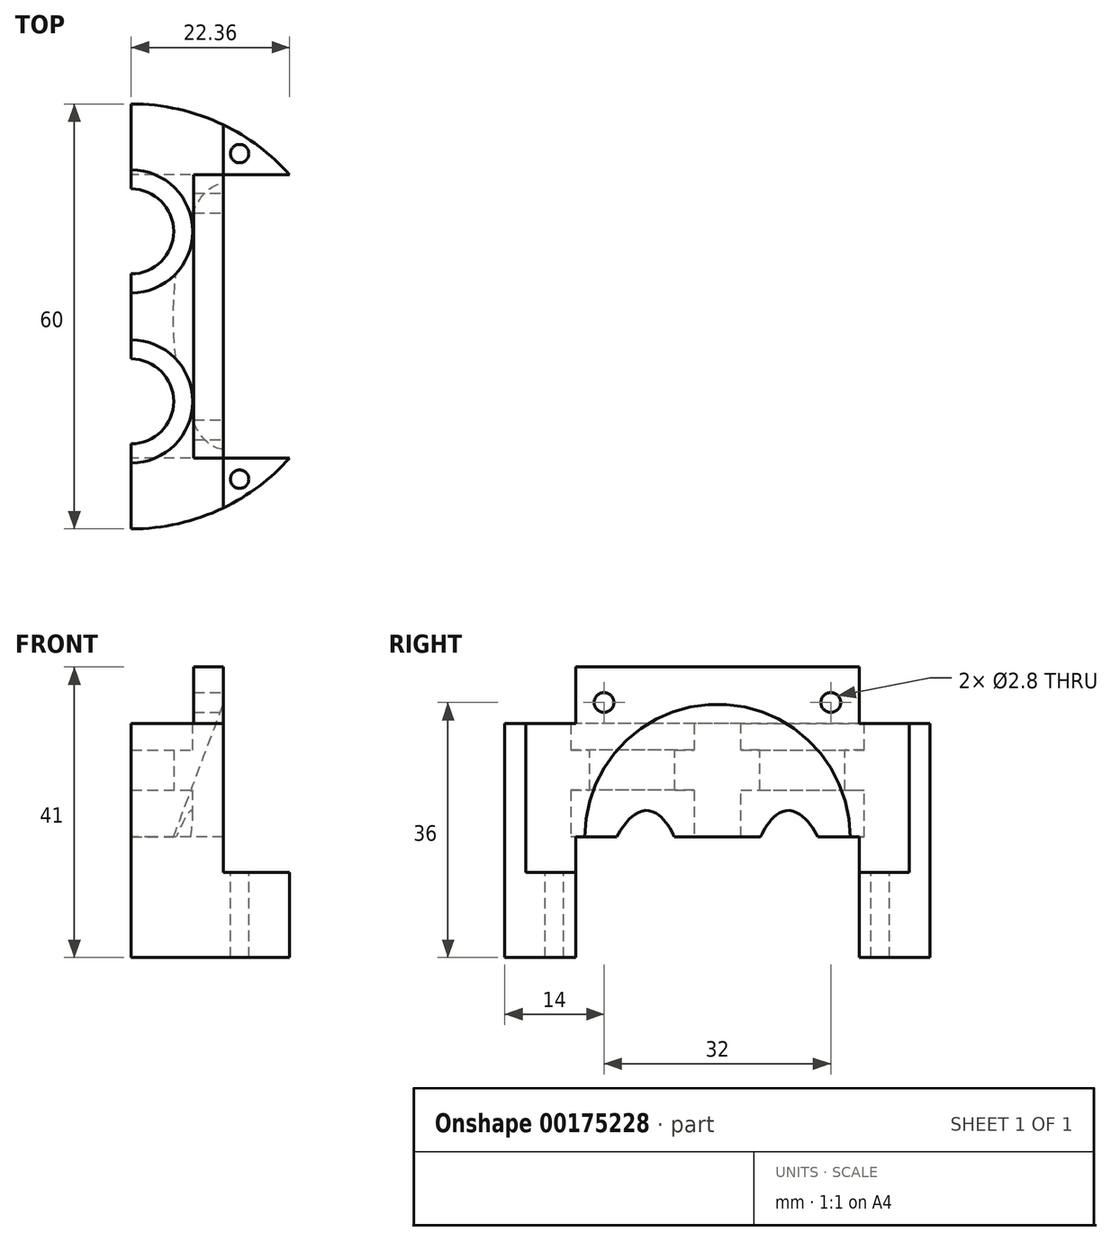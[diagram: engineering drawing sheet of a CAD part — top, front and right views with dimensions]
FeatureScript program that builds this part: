
annotation { "Feature Type Name" : "Feature", "Feature Type Description" : "" }
export const myFeature = defineFeature(function(context is Context, id is Id, definition is map)
    precondition{}
    {
        {
            var Q0;
            Q0=qCreatedBy(makeId("Top.planeOp"),FACE);
            var sketch = newSketch(context, id + "F0", { "sketchPlane" : qUnion([Q0])});
            skLineSegment(sketch, "E0.bottom", {"start": v(-13, -12) * mm, "end": v(13, -12) * mm});
            skLineSegment(sketch, "E0.top", {"start": v(-13, 12) * mm, "end": v(13, 12) * mm});
            skLineSegment(sketch, "E0.left", {"start": v(-13, -12) * mm, "end": v(-13, 12) * mm});
            skLineSegment(sketch, "E0.right", {"start": v(13, -12) * mm, "end": v(13, 12) * mm});
            skPoint(sketch, "E0.middle", {"position": v(0, 0) * mm});
            skCircle(sketch, "E1", {"center": v(0, 0) * mm, "radius": 20 * mm, "construction": true});
            skLineSegment(sketch, "E2", {"start": v(-31.1, 0) * mm, "end": v(39.02, 0) * mm, "construction": true});
            skCircle(sketch, "E3", {"center": v(0, 0) * mm, "radius": 30 * mm});
            skCircle(sketch, "E4", {"center": v(0, 12) * mm, "radius": 6 * mm});
            skCircle(sketch, "E5", {"center": v(0, -12) * mm, "radius": 6 * mm});
            skLineSegment(sketch, "E6.bottom", {"start": v(-13, 27.04) * mm, "end": v(13, 27.04) * mm});
            skLineSegment(sketch, "E6.top", {"start": v(-13, -27.04) * mm, "end": v(13, -27.04) * mm});
            skLineSegment(sketch, "E6.left", {"start": v(-13, 27.04) * mm, "end": v(-13, -27.04) * mm});
            skLineSegment(sketch, "E6.right", {"start": v(13, 27.04) * mm, "end": v(13, -27.04) * mm});
            skSolve(sketch);
        }
        {
            var Q0;
            {var subQ0=sQuery(id+"F0.wireOp",EDGE,"E6.bottom");Q0=makeQuery(id+"F0.imprint","IMPRINT",FACE,{"disambiguationData":[TD([[makeQuery(id+"F0.imprint","IMPRINT",EDGE,{"derivedFrom":subQ0}),1.0]])]});}
            var Q1;
            {var subQ0=sQuery(id+"F0.wireOp",EDGE,"E6.top");Q1=makeQuery(id+"F0.imprint","IMPRINT",FACE,{"disambiguationData":[TD([[makeQuery(id+"F0.imprint","IMPRINT",EDGE,{"derivedFrom":subQ0}),-1.0]])]});}
            var Q2;
            {var subQ0=sQuery(id+"F0.wireOp",EDGE,"E6.top");Q2=makeQuery(id+"F0.imprint","IMPRINT",FACE,{"disambiguationData":[TD([[makeQuery(id+"F0.imprint","IMPRINT",EDGE,{"derivedFrom":subQ0}),1.0]])]});}
            var Q3;
            {var subQ6=sQuery(id+"F0.wireOp",EDGE,"E0.bottom");var subQ9=sQuery(id+"F0.wireOp",EDGE,"E6.left");var subQ13=makeQuery(id+"F0.imprint","INTERSECT",VERTEX,{"derivedFrom":[subQ6,subQ9]});Q3=makeQuery(id+"F0.imprint","IMPRINT",FACE,{"disambiguationData":[TD([[makeQuery(id+"F0.imprint","IMPRINT",EDGE,{"disambiguationData":[TD([[subQ13,-1.0]])],"derivedFrom":subQ6}),1.0]])]});}
            var Q4;
            {var subQ0=sQuery(id+"F0.wireOp",EDGE,"E6.bottom");Q4=makeQuery(id+"F0.imprint","IMPRINT",FACE,{"disambiguationData":[TD([[makeQuery(id+"F0.imprint","IMPRINT",EDGE,{"derivedFrom":subQ0}),-1.0]])]});}
            extrude(context, id + "F1", {"entities" : qUnion([Q0, Q1, Q2, Q3, Q4]), "depth" : 33 * mm});
        }
        {
            var Q0;
            Q0=qCreatedBy(makeId("Top.planeOp"),FACE);
            var sketch = newSketch(context, id + "F2", { "sketchPlane" : qUnion([Q0])});
            skCircle(sketch, "E7", {"center": v(0, 0) * mm, "radius": 30 * mm});
            skCircle(sketch, "E8", {"center": v(-26.68, -13.72) * mm, "radius": 7.63 * mm});
            skLineSegment(sketch, "E9", {"start": v(-22.36, -20) * mm, "end": v(-12.88, -20) * mm});
            skLineSegment(sketch, "E10", {"start": v(-12.88, -20) * mm, "end": v(22.36, -20) * mm});
            skLineSegment(sketch, "E11", {"start": v(22.36, -20) * mm, "end": v(-53.5, 0) * mm, "construction": true});
            skLineSegment(sketch, "E12", {"start": v(-53.5, 0) * mm, "end": v(57.64, 0) * mm, "construction": true});
            skLineSegment(sketch, "E13.MirrorCS", {"start": v(-12.88, 20) * mm, "end": v(22.36, 20) * mm});
            skLineSegment(sketch, "E14.MirrorCS", {"start": v(-22.36, 20) * mm, "end": v(-12.88, 20) * mm});
            skSolve(sketch);
        }
        {
            var Q0;
            {var subQ0=sQuery(id+"F2.wireOp",EDGE,"E13.MirrorCS");Q0=makeQuery(id+"F2.imprint","IMPRINT",FACE,{"disambiguationData":[TD([[makeQuery(id+"F2.imprint","IMPRINT",EDGE,{"derivedFrom":subQ0}),1.0]])]});}
            var Q1;
            {var subQ0=sQuery(id+"F2.wireOp",EDGE,"E9");Q1=makeQuery(id+"F2.imprint","IMPRINT",FACE,{"disambiguationData":[TD([[makeQuery(id+"F2.imprint","IMPRINT",EDGE,{"derivedFrom":subQ0}),-1.0]])]});}
            extrude(context, id + "F3", {"entities" : qUnion([Q0, Q1]), "operationType" : NewBodyOperationType.ADD, "depth" : 12 * mm});
        }
        {
            var Q0;
            Q0=makeQuery(id+"F1.opExtrude","CAP_FACE",FACE,{"disambiguationData":[OSD([sQuery(id+"F0.wireOp",EDGE,"E3"),sQuery(id+"F0.wireOp",EDGE,"E4"),sQuery(id+"F0.wireOp",EDGE,"E5"),sQuery(id+"F0.wireOp",EDGE,"E6.left"),sQuery(id+"F0.wireOp",EDGE,"E6.right")])],"isStart":false});
            var sketch = newSketch(context, id + "F4", { "sketchPlane" : qUnion([Q0])});
            skLineSegment(sketch, "E15", {"start": v(0, 35.89) * mm, "end": v(0, -37.95) * mm});
            skPoint(sketch, "E15.endSnap0", {"position": v(0, 30) * mm});
            skLineSegment(sketch, "E16", {"start": v(0, -37.95) * mm, "end": v(28.6, -37.95) * mm});
            skLineSegment(sketch, "E17", {"start": v(28.6, -37.95) * mm, "end": v(28.6, 36.6) * mm});
            skLineSegment(sketch, "E18", {"start": v(28.6, 36.6) * mm, "end": v(0, 36.6) * mm});
            skLineSegment(sketch, "E19", {"start": v(0, 36.6) * mm, "end": v(0, 33.04) * mm});
            skSolve(sketch);
        }
        {
            var Q0;
            Q0=makeQuery(id+"F1.opExtrude","SWEPT_FACE",FACE,{"disambiguationData":[OSD([sQuery(id+"F0.wireOp",EDGE,"E6.left")])]});
            var sketch = newSketch(context, id + "F5", { "sketchPlane" : qUnion([Q0])});
            skLineSegment(sketch, "E20.bottom", {"start": v(-20, 0) * mm, "end": v(20, 0) * mm});
            skLineSegment(sketch, "E20.top", {"start": v(-20, 17) * mm, "end": v(20, 17) * mm});
            skLineSegment(sketch, "E20.left", {"start": v(-20, 0) * mm, "end": v(-20, 17) * mm});
            skLineSegment(sketch, "E20.right", {"start": v(20, 0) * mm, "end": v(20, 17) * mm});
            skSolve(sketch);
        }
        {
            var Q0;
            {var subQ5=sQuery(id+"F5.wireOp",EDGE,"E20.bottom");Q0=makeQuery(id+"F5.imprint","IMPRINT",FACE,{"disambiguationData":[TD([[makeQuery(id+"F5.imprint","IMPRINT",EDGE,{"derivedFrom":subQ5}),1.0]])]});}
            extrude(context, id + "F6", {"entities" : qUnion([Q0]), "operationType" : NewBodyOperationType.REMOVE, "endBound" : BoundingType.THROUGH_ALL, "oppositeDirection" : true, "depth" : 25 * mm});
        }
        {
            var Q0;
            Q0=makeQuery(id+"F6.boolean.opBoolean","COPY",FACE,{"derivedFrom":makeQuery(id+"F6.opExtrude","SWEPT_FACE",FACE,{"disambiguationData":[OSD([sQuery(id+"F5.wireOp",EDGE,"E20.top")])]})});
            var sketch = newSketch(context, id + "F7", { "sketchPlane" : qUnion([Q0])});
            skCircle(sketch, "E21", {"center": v(0, 12) * mm, "radius": 11.29 * mm, "construction": true});
            skCircle(sketch, "E22", {"center": v(0, -12) * mm, "radius": 11.29 * mm, "construction": true});
            skCircle(sketch, "E23", {"center": v(0, 12) * mm, "radius": 11.29 * mm});
            skCircle(sketch, "E24", {"center": v(0, -12) * mm, "radius": 11.29 * mm});
            skSolve(sketch);
        }
        {
            var Q0;
            Q0=makeQuery(id+"F7.imprint","IMPRINT",FACE,{"disambiguationData":[TD([[makeQuery(id+"F7.imprint","IMPRINT",EDGE,{"derivedFrom":makeQuery(id+"F6.boolean.opBoolean","INTERSECT",EDGE,{"derivedFrom":[makeQuery(id+"F1.opExtrude","SWEPT_FACE",FACE,{"disambiguationData":[OSD([sQuery(id+"F0.wireOp",EDGE,"E4")])]}),makeQuery(id+"F6.opExtrude","SWEPT_FACE",FACE,{"disambiguationData":[OSD([sQuery(id+"F5.wireOp",EDGE,"E20.top")])]})]})}),1.0]])]});
            var Q1;
            Q1=makeQuery(id+"F7.imprint","IMPRINT",FACE,{"disambiguationData":[TD([[makeQuery(id+"F7.imprint","IMPRINT",EDGE,{"derivedFrom":makeQuery(id+"F6.boolean.opBoolean","INTERSECT",EDGE,{"derivedFrom":[makeQuery(id+"F1.opExtrude","SWEPT_FACE",FACE,{"disambiguationData":[OSD([sQuery(id+"F0.wireOp",EDGE,"E5")])]}),makeQuery(id+"F6.opExtrude","SWEPT_FACE",FACE,{"disambiguationData":[OSD([sQuery(id+"F5.wireOp",EDGE,"E20.top")])]})]})}),1.0]])]});
            var Q2;
            {var subQ0=sQuery(id+"F7.wireOp",EDGE,"E23");var subQ1=makeQuery(id+"F6.boolean.opBoolean","COPY",EDGE,{"derivedFrom":makeQuery(id+"F6.opExtrude","SWEPT_EDGE",EDGE,{"disambiguationData":[OSD([sQuery(id+"F5.wireOp",EDGE,"E20.top"),sQuery(id+"F5.wireOp",EDGE,"E20.right")])]})});var subQ2=makeQuery(id+"F7.imprint","INTERSECT",VERTEX,{"disambiguationData":[OD(0.0)],"derivedFrom":[subQ1,subQ0]});Q2=makeQuery(id+"F7.imprint","IMPRINT",FACE,{"disambiguationData":[TD([[makeQuery(id+"F7.imprint","IMPRINT",EDGE,{"disambiguationData":[TD([[subQ2,1.0]])],"derivedFrom":subQ0}),1.0]])]});}
            var Q3;
            {var subQ0=sQuery(id+"F7.wireOp",EDGE,"E24");var subQ1=makeQuery(id+"F6.boolean.opBoolean","COPY",EDGE,{"derivedFrom":makeQuery(id+"F6.opExtrude","SWEPT_EDGE",EDGE,{"disambiguationData":[OSD([sQuery(id+"F5.wireOp",EDGE,"E20.top"),sQuery(id+"F5.wireOp",EDGE,"E20.left")])]})});var subQ2=makeQuery(id+"F7.imprint","INTERSECT",VERTEX,{"disambiguationData":[OD(0.0)],"derivedFrom":[subQ1,subQ0]});Q3=makeQuery(id+"F7.imprint","IMPRINT",FACE,{"disambiguationData":[TD([[makeQuery(id+"F7.imprint","IMPRINT",EDGE,{"disambiguationData":[TD([[subQ2,-1.0]])],"derivedFrom":subQ0}),1.0]])]});}
            var Q4;
            {var subQ1=sQuery(id+"F5.wireOp",EDGE,"E20.top");Q4=makeQuery(id+"F7.imprint","IMPRINT",FACE,{"disambiguationData":[TD([[makeQuery(id+"F7.imprint","IMPRINT",EDGE,{"derivedFrom":makeQuery(id+"F6.boolean.opBoolean","INTERSECT",EDGE,{"derivedFrom":[makeQuery(id+"F1.opExtrude","SWEPT_FACE",FACE,{"disambiguationData":[OSD([sQuery(id+"F0.wireOp",EDGE,"E5")])]}),makeQuery(id+"F6.opExtrude","SWEPT_FACE",FACE,{"disambiguationData":[OSD([subQ1])]})]})}),-1.0]])]});}
            extrude(context, id + "F8", {"entities" : qUnion([Q0, Q1, Q2, Q3, Q4]), "operationType" : NewBodyOperationType.REMOVE, "endBound" : BoundingType.THROUGH_ALL, "depth" : 25 * mm});
        }
        {
            var Q0;
            {var subQ0=sQuery(id+"F0.wireOp",EDGE,"E6.right");var subQ1=makeQuery(id+"F1.opExtrude","CAP_EDGE",EDGE,{"disambiguationData":[OSD([subQ0])],"isStart":false});Q0=makeQuery(id+"F4.imprint","IMPRINT",FACE,{"disambiguationData":[TD([[makeQuery(id+"F4.imprint","IMPRINT",EDGE,{"derivedFrom":subQ1}),-1.0]])]});}
            var sketch = newSketch(context, id + "F9", { "sketchPlane" : qUnion([Q0])});
            skLineSegment(sketch, "E25.bottom", {"start": v(13, 20) * mm, "end": v(-13, 20) * mm});
            skLineSegment(sketch, "E25.top", {"start": v(13, -20) * mm, "end": v(-13, -20) * mm});
            skLineSegment(sketch, "E25.left", {"start": v(13, 20) * mm, "end": v(13, -20) * mm});
            skLineSegment(sketch, "E25.right", {"start": v(-13, 20) * mm, "end": v(-13, -20) * mm});
            skPoint(sketch, "E25.middle", {"position": v(0, 0) * mm});
            skLineSegment(sketch, "E26.bottom", {"start": v(8.83, 20) * mm, "end": v(17.17, 20) * mm});
            skLineSegment(sketch, "E26.top", {"start": v(8.83, -20) * mm, "end": v(17.17, -20) * mm});
            skLineSegment(sketch, "E26.left", {"start": v(8.83, 20) * mm, "end": v(8.83, -20) * mm});
            skLineSegment(sketch, "E26.right", {"start": v(17.17, 20) * mm, "end": v(17.17, -20) * mm});
            skPoint(sketch, "E26.middle", {"position": v(13, 0) * mm});
            skSolve(sketch);
        }
        {
            var Q0;
            {var subQ0=sQuery(id+"F9.wireOp",EDGE,"E26.left");Q0=makeQuery(id+"F9.imprint","IMPRINT",FACE,{"disambiguationData":[TD([[makeQuery(id+"F9.imprint","IMPRINT",EDGE,{"derivedFrom":subQ0}),1.0]])]});}
            extrude(context, id + "F10", {"entities" : qUnion([Q0]), "operationType" : NewBodyOperationType.ADD, "depth" : 8 * mm});
        }
        {
            var Q0;
            {var subQ0=sQuery(id+"F0.wireOp",EDGE,"E6.right");Q0=makeQuery(id+"F10.boolean.opBoolean","MERGE",FACE,{"derivedFrom":[makeQuery(id+"F1.opExtrude","SWEPT_FACE",FACE,{"disambiguationData":[OSD([subQ0])]}),makeQuery(id+"F10.opExtrude","SWEPT_FACE",FACE,{"disambiguationData":[OSD([subQ0])]})]});}
            var sketch = newSketch(context, id + "F11", { "sketchPlane" : qUnion([Q0])});
            skLineSegment(sketch, "E27.bottom", {"start": v(-20, 41) * mm, "end": v(20, 41) * mm});
            skLineSegment(sketch, "E27.top", {"start": v(-20, 0) * mm, "end": v(20, 0) * mm});
            skLineSegment(sketch, "E27.left", {"start": v(-20, 41) * mm, "end": v(-20, 0) * mm});
            skLineSegment(sketch, "E27.right", {"start": v(20, 41) * mm, "end": v(20, 0) * mm});
            skLineSegment(sketch, "E28", {"start": v(-20, 36) * mm, "end": v(20, 36) * mm, "construction": true});
            skCircle(sketch, "E29", {"center": v(-16, 36) * mm, "radius": 1.4 * mm});
            skCircle(sketch, "E30", {"center": v(16, 36) * mm, "radius": 1.4 * mm});
            skSolve(sketch);
        }
        {
            var Q0;
            Q0=makeQuery(id+"F11.imprint","IMPRINT",FACE,{"disambiguationData":[TD([[makeQuery(id+"F11.imprint","IMPRINT",EDGE,{"derivedFrom":sQuery(id+"F11.wireOp",EDGE,"E29")}),1.0]])]});
            var Q1;
            Q1=makeQuery(id+"F11.imprint","IMPRINT",FACE,{"disambiguationData":[TD([[makeQuery(id+"F11.imprint","IMPRINT",EDGE,{"derivedFrom":sQuery(id+"F11.wireOp",EDGE,"E30")}),1.0]])]});
            extrude(context, id + "F12", {"entities" : qUnion([Q0, Q1]), "operationType" : NewBodyOperationType.REMOVE, "endBound" : BoundingType.THROUGH_ALL, "oppositeDirection" : true, "depth" : 25 * mm});
        }
        {
            var Q0;
            {var subQ0=sQuery(id+"F0.wireOp",EDGE,"E6.left");var subQ1=makeQuery(id+"F1.opExtrude","CAP_EDGE",EDGE,{"disambiguationData":[OSD([subQ0])],"isStart":false});Q0=makeQuery(id+"F4.imprint","IMPRINT",FACE,{"disambiguationData":[TD([[makeQuery(id+"F4.imprint","IMPRINT",EDGE,{"derivedFrom":subQ1}),1.0]])]});}
            var sketch = newSketch(context, id + "F13", { "sketchPlane" : qUnion([Q0])});
            skLineSegment(sketch, "E31", {"start": v(0, 33.3) * mm, "end": v(0, -31.46) * mm});
            skLineSegment(sketch, "E32", {"start": v(0, -31.46) * mm, "end": v(26.28, -31.46) * mm});
            skLineSegment(sketch, "E33", {"start": v(26.28, -31.46) * mm, "end": v(26.28, 32.75) * mm});
            skLineSegment(sketch, "E34", {"start": v(26.28, 32.75) * mm, "end": v(0, 32.75) * mm});
            skLineSegment(sketch, "E35.MirrorCS", {"start": v(-26.28, -31.46) * mm, "end": v(-26.28, 32.75) * mm});
            skLineSegment(sketch, "E36.MirrorCS", {"start": v(-26.28, 32.75) * mm, "end": v(0, 32.75) * mm});
            skLineSegment(sketch, "E37.MirrorCS", {"start": v(0, -31.46) * mm, "end": v(-26.28, -31.46) * mm});
            skSolve(sketch);
        }
        {
            var Q0;
            Q0=makeQuery(id+"F13.imprint","IMPRINT",FACE,{"disambiguationData":[TD([[makeQuery(id+"F13.imprint","IMPRINT",EDGE,{"derivedFrom":sQuery(id+"F13.wireOp",EDGE,"E35.MirrorCS")}),-1.0]])]});
            var Q1;
            {var subQ0=sQuery(id+"F0.wireOp",EDGE,"E6.left");var subQ1=makeQuery(id+"F1.opExtrude","CAP_EDGE",EDGE,{"disambiguationData":[OSD([subQ0])],"isStart":false});Q1=makeQuery(id+"F4.imprint","IMPRINT",FACE,{"disambiguationData":[TD([[makeQuery(id+"F4.imprint","IMPRINT",EDGE,{"derivedFrom":subQ1}),1.0]])]});}
            extrude(context, id + "F14", {"entities" : qUnion([Q0, Q1]), "operationType" : NewBodyOperationType.REMOVE, "endBound" : BoundingType.THROUGH_ALL, "oppositeDirection" : true, "depth" : 25 * mm});
        }
        {
            var Q0;
            {var subQ0=sQuery(id+"F4.wireOp",EDGE,"E15");Q0=makeQuery(id+"F14.boolean.opBoolean","COPY",FACE,{"derivedFrom":makeQuery(id+"F14.opExtrude","SWEPT_FACE",FACE,{"disambiguationData":[OSD([subQ0]),TDD([makeQuery(id+"F4.imprint","IMPRINT",EDGE,{"disambiguationData":[TD([[makeQuery(id+"F4.imprint","INTERSECT",VERTEX,{"disambiguationData":[OD(1.0)],"derivedFrom":[makeQuery(id+"F1.opExtrude","CAP_EDGE",EDGE,{"disambiguationData":[OSD([sQuery(id+"F0.wireOp",EDGE,"E4")])],"isStart":false}),subQ0]}),-1.0]])],"derivedFrom":subQ0})])]})});}
            var sketch = newSketch(context, id + "F15", { "sketchPlane" : qUnion([Q0])});
            skLineSegment(sketch, "E38.bottom", {"start": v(-6, 17) * mm, "end": v(6, 17) * mm});
            skLineSegment(sketch, "E38.top", {"start": v(-6, 49) * mm, "end": v(6, 49) * mm});
            skLineSegment(sketch, "E38.left", {"start": v(-6, 17) * mm, "end": v(-6, 49) * mm});
            skLineSegment(sketch, "E38.right", {"start": v(6, 17) * mm, "end": v(6, 49) * mm});
            skPoint(sketch, "E38.middle", {"position": v(0, 33) * mm});
            skLineSegment(sketch, "E39.bottom", {"start": v(12, 17) * mm, "end": v(-12, 17) * mm});
            skLineSegment(sketch, "E39.top", {"start": v(12, 49) * mm, "end": v(-12, 49) * mm});
            skLineSegment(sketch, "E39.left", {"start": v(12, 17) * mm, "end": v(12, 49) * mm});
            skLineSegment(sketch, "E39.right", {"start": v(-12, 17) * mm, "end": v(-12, 49) * mm});
            skLineSegment(sketch, "E40.bottom", {"start": v(12, 29.31) * mm, "end": v(-12, 29.31) * mm});
            skLineSegment(sketch, "E40.top", {"start": v(12, 36.7) * mm, "end": v(-12, 36.7) * mm});
            skLineSegment(sketch, "E40.left", {"start": v(12, 29.31) * mm, "end": v(12, 36.7) * mm});
            skLineSegment(sketch, "E40.right", {"start": v(-12, 29.31) * mm, "end": v(-12, 36.7) * mm});
            skLineSegment(sketch, "E41.bottom", {"start": v(-12, 33) * mm, "end": v(-3.3, 33) * mm});
            skLineSegment(sketch, "E41.top", {"start": v(-12, 29.31) * mm, "end": v(-3.3, 29.31) * mm});
            skLineSegment(sketch, "E41.left", {"start": v(-12, 33) * mm, "end": v(-12, 29.31) * mm});
            skLineSegment(sketch, "E41.right", {"start": v(-3.3, 33) * mm, "end": v(-3.3, 29.31) * mm});
            skLineSegment(sketch, "E42.bottom", {"start": v(-12, 23.6) * mm, "end": v(-3.31, 23.6) * mm});
            skLineSegment(sketch, "E42.top", {"start": v(-12, 17) * mm, "end": v(-3.3, 17) * mm});
            skLineSegment(sketch, "E42.left", {"start": v(-12, 23.6) * mm, "end": v(-12, 17) * mm});
            skLineSegment(sketch, "E42.right", {"start": v(-3.31, 23.6) * mm, "end": v(-3.31, 17) * mm});
            skLineSegment(sketch, "E43", {"start": v(-3.3, 33) * mm, "end": v(-12, 33) * mm});
            skLineSegment(sketch, "E44", {"start": v(-3.31, 23.6) * mm, "end": v(-12, 23.6) * mm});
            skSolve(sketch);
        }
        {
            var Q0;
            {var subQ5=sQuery(id+"F15.wireOp",EDGE,"E41.right");Q0=makeQuery(id+"F15.imprint","IMPRINT",FACE,{"disambiguationData":[TD([[makeQuery(id+"F15.imprint","IMPRINT",EDGE,{"derivedFrom":subQ5}),-1.0]])]});}
            var Q1;
            {var subQ5=sQuery(id+"F15.wireOp",EDGE,"E42.right");Q1=makeQuery(id+"F15.imprint","IMPRINT",FACE,{"disambiguationData":[TD([[makeQuery(id+"F15.imprint","IMPRINT",EDGE,{"derivedFrom":subQ5}),-1.0]])]});}
            var Q2;
            Q2=sQuery(id+"F15.wireOp",EDGE,"E39.right");
            revolve(context, id + "F16", {"operationType" : NewBodyOperationType.REMOVE, "entities" : qUnion([Q0, Q1]), "axis" : qUnion([Q2]), "revolveType" : RevolveType.FULL, "oppositeDirection" : true});
        }
        {
            var Q0;
            {var subQ0=sQuery(id+"F4.wireOp",EDGE,"E15");Q0=makeQuery(id+"F14.boolean.opBoolean","COPY",FACE,{"derivedFrom":makeQuery(id+"F14.opExtrude","SWEPT_FACE",FACE,{"disambiguationData":[OSD([subQ0]),TDD([makeQuery(id+"F4.imprint","IMPRINT",EDGE,{"disambiguationData":[TD([[makeQuery(id+"F4.imprint","INTERSECT",VERTEX,{"disambiguationData":[OD(1.0)],"derivedFrom":[makeQuery(id+"F1.opExtrude","CAP_EDGE",EDGE,{"disambiguationData":[OSD([sQuery(id+"F0.wireOp",EDGE,"E4")])],"isStart":false}),subQ0]}),-1.0]])],"derivedFrom":subQ0})])]})});}
            var sketch = newSketch(context, id + "F17", { "sketchPlane" : qUnion([Q0])});
            skLineSegment(sketch, "E45.bottom", {"start": v(-6, 29.31) * mm, "end": v(6, 29.31) * mm});
            skLineSegment(sketch, "E45.top", {"start": v(-6, 23.6) * mm, "end": v(6, 23.6) * mm});
            skLineSegment(sketch, "E45.left", {"start": v(-6, 29.31) * mm, "end": v(-6, 23.6) * mm});
            skLineSegment(sketch, "E45.right", {"start": v(6, 29.31) * mm, "end": v(6, 23.6) * mm});
            skLineSegment(sketch, "E46.bottom", {"start": v(0, 23.6) * mm, "end": v(12, 23.6) * mm});
            skLineSegment(sketch, "E46.top", {"start": v(0, 17) * mm, "end": v(12, 17) * mm});
            skLineSegment(sketch, "E46.left", {"start": v(0, 23.6) * mm, "end": v(0, 17) * mm});
            skLineSegment(sketch, "E46.right", {"start": v(12, 23.6) * mm, "end": v(12, 17) * mm});
            skLineSegment(sketch, "E47.bottom", {"start": v(12, 23.6) * mm, "end": v(3.3, 23.6) * mm});
            skLineSegment(sketch, "E47.top", {"start": v(12, 17) * mm, "end": v(3.3, 17) * mm});
            skLineSegment(sketch, "E47.right", {"start": v(3.3, 23.6) * mm, "end": v(3.3, 17) * mm});
            skLineSegment(sketch, "E48.bottom", {"start": v(3.3, 29.31) * mm, "end": v(12, 29.31) * mm});
            skLineSegment(sketch, "E48.top", {"start": v(3.3, 33) * mm, "end": v(12, 33) * mm});
            skLineSegment(sketch, "E48.left", {"start": v(3.3, 29.31) * mm, "end": v(3.3, 33) * mm});
            skLineSegment(sketch, "E48.right", {"start": v(12, 29.31) * mm, "end": v(12, 33) * mm});
            skLineSegment(sketch, "E49", {"start": v(12, 33) * mm, "end": v(12, 15.28) * mm});
            skLineSegment(sketch, "E50", {"start": v(12, 15.28) * mm, "end": v(12, 23.6) * mm});
            skLineSegment(sketch, "E51", {"start": v(12, 17) * mm, "end": v(12, 29.31) * mm});
            skLineSegment(sketch, "E52", {"start": v(12, 33) * mm, "end": v(12, 29.31) * mm});
            skSolve(sketch);
        }
        {
            var Q0;
            {var subQ6=sQuery(id+"F17.wireOp",EDGE,"E48.left");Q0=makeQuery(id+"F17.imprint","IMPRINT",FACE,{"disambiguationData":[TD([[makeQuery(id+"F17.imprint","IMPRINT",EDGE,{"derivedFrom":subQ6}),-1.0]])]});}
            var Q1;
            {var subQ5=sQuery(id+"F17.wireOp",EDGE,"E47.right");Q1=makeQuery(id+"F17.imprint","IMPRINT",FACE,{"disambiguationData":[TD([[makeQuery(id+"F17.imprint","IMPRINT",EDGE,{"derivedFrom":subQ5}),1.0]])]});}
            var Q2;
            Q2=sQuery(id+"F17.wireOp",EDGE,"E49");
            revolve(context, id + "F18", {"operationType" : NewBodyOperationType.REMOVE, "entities" : qUnion([Q0, Q1]), "axis" : qUnion([Q2]), "revolveType" : RevolveType.FULL, "oppositeDirection" : true});
        }
        {
            var Q0;
            {var subQ0=sQuery(id+"F0.wireOp",EDGE,"E6.right");Q0=makeQuery(id+"F10.boolean.opBoolean","MERGE",FACE,{"derivedFrom":[makeQuery(id+"F1.opExtrude","SWEPT_FACE",FACE,{"disambiguationData":[OSD([subQ0])]}),makeQuery(id+"F10.opExtrude","SWEPT_FACE",FACE,{"disambiguationData":[OSD([subQ0])]})]});}
            var sketch = newSketch(context, id + "F19", { "sketchPlane" : qUnion([Q0])});
            skCircle(sketch, "E53", {"center": v(0, 17) * mm, "radius": 18.74 * mm});
            skSolve(sketch);
        }
        {
            var Q0;
            Q0=qCreatedBy(makeId("Front.planeOp"),FACE);
            var sketch = newSketch(context, id + "F20", { "sketchPlane" : qUnion([Q0])});
            skLineSegment(sketch, "E54", {"start": v(17.93, 25.94) * mm, "end": v(5.67, -6.7) * mm});
            skSolve(sketch);
        }
        {
            var Q0;
            {var subQ0=sQuery(id+"F19.wireOp",EDGE,"E53");var subQ1=makeQuery(id+"F6.boolean.opBoolean","INTERSECT",EDGE,{"derivedFrom":[makeQuery(id+"F1.opExtrude","SWEPT_FACE",FACE,{"disambiguationData":[OSD([sQuery(id+"F0.wireOp",EDGE,"E6.right")])]}),makeQuery(id+"F6.opExtrude","SWEPT_FACE",FACE,{"disambiguationData":[OSD([sQuery(id+"F5.wireOp",EDGE,"E20.top")])]})]});var subQ2=makeQuery(id+"F19.imprint","INTERSECT",VERTEX,{"disambiguationData":[OD(0.0)],"derivedFrom":[subQ1,subQ0]});Q0=makeQuery(id+"F19.imprint","IMPRINT",FACE,{"disambiguationData":[TD([[makeQuery(id+"F19.imprint","IMPRINT",EDGE,{"disambiguationData":[TD([[subQ2,-1.0]])],"derivedFrom":subQ0}),1.0]])]});}
            var Q1;
            {var subQ0=sQuery(id+"F19.wireOp",EDGE,"E53");var subQ1=makeQuery(id+"F6.boolean.opBoolean","INTERSECT",EDGE,{"derivedFrom":[makeQuery(id+"F1.opExtrude","SWEPT_FACE",FACE,{"disambiguationData":[OSD([sQuery(id+"F0.wireOp",EDGE,"E6.right")])]}),makeQuery(id+"F6.opExtrude","SWEPT_FACE",FACE,{"disambiguationData":[OSD([sQuery(id+"F5.wireOp",EDGE,"E20.top")])]})]});var subQ2=makeQuery(id+"F19.imprint","INTERSECT",VERTEX,{"disambiguationData":[OD(0.0)],"derivedFrom":[subQ1,subQ0]});Q1=makeQuery(id+"F19.imprint","IMPRINT",FACE,{"disambiguationData":[TD([[makeQuery(id+"F19.imprint","IMPRINT",EDGE,{"disambiguationData":[TD([[subQ2,1.0]])],"derivedFrom":subQ0}),1.0]])]});}
            var Q2;
            Q2=sQuery(id+"F20.wireOp",EDGE,"E54");
            sweep(context, id + "F21", {"operationType" : NewBodyOperationType.REMOVE, "profiles" : qUnion([Q0, Q1]), "path" : qUnion([Q2])});
        }
        {
            var Q0;
            Q0=makeQuery(id+"F10.opExtrude","CAP_FACE",FACE,{"disambiguationData":[OSD([sQuery(id+"F0.wireOp",EDGE,"E6.right"),sQuery(id+"F9.wireOp",EDGE,"E26.bottom"),sQuery(id+"F9.wireOp",EDGE,"E26.top"),sQuery(id+"F9.wireOp",EDGE,"E26.left")])],"isStart":false});
            var sketch = newSketch(context, id + "F22", { "sketchPlane" : qUnion([Q0])});
            skLineSegment(sketch, "E55.bottom", {"start": v(15.3, 22.98) * mm, "end": v(10.7, 22.98) * mm});
            skLineSegment(sketch, "E55.top", {"start": v(15.3, -22.98) * mm, "end": v(10.7, -22.98) * mm});
            skLineSegment(sketch, "E55.left", {"start": v(15.3, 22.98) * mm, "end": v(15.3, -22.98) * mm});
            skLineSegment(sketch, "E55.right", {"start": v(10.7, 22.98) * mm, "end": v(10.7, -22.98) * mm});
            skPoint(sketch, "E55.middle", {"position": v(13, 0) * mm});
            skCircle(sketch, "E56", {"center": v(15.3, 22.98) * mm, "radius": 1.3 * mm});
            skCircle(sketch, "E57", {"center": v(15.3, -22.98) * mm, "radius": 1.3 * mm});
            skSolve(sketch);
        }
        {
            var Q0;
            {var subQ0=sQuery(id+"F22.wireOp",EDGE,"E55.left");var subQ1=sQuery(id+"F22.wireOp",EDGE,"E55.bottom");var subQ2=makeQuery(id+"F22.imprint","INTERSECT",VERTEX,{"derivedFrom":[subQ1,subQ0]});Q0=makeQuery(id+"F22.imprint","IMPRINT",FACE,{"disambiguationData":[TD([[makeQuery(id+"F22.imprint","IMPRINT",EDGE,{"disambiguationData":[TD([[subQ2,-1.0]])],"derivedFrom":subQ1}),1.0]])]});}
            var Q1;
            {var subQ0=sQuery(id+"F22.wireOp",EDGE,"E55.left");var subQ1=sQuery(id+"F22.wireOp",EDGE,"E55.bottom");var subQ2=makeQuery(id+"F22.imprint","INTERSECT",VERTEX,{"derivedFrom":[subQ1,subQ0]});Q1=makeQuery(id+"F22.imprint","IMPRINT",FACE,{"disambiguationData":[TD([[makeQuery(id+"F22.imprint","IMPRINT",EDGE,{"disambiguationData":[TD([[subQ2,-1.0]])],"derivedFrom":subQ1}),-1.0]])]});}
            var Q2;
            {var subQ0=sQuery(id+"F22.wireOp",EDGE,"E55.left");var subQ1=sQuery(id+"F22.wireOp",EDGE,"E55.top");var subQ2=makeQuery(id+"F22.imprint","INTERSECT",VERTEX,{"derivedFrom":[subQ1,subQ0]});Q2=makeQuery(id+"F22.imprint","IMPRINT",FACE,{"disambiguationData":[TD([[makeQuery(id+"F22.imprint","IMPRINT",EDGE,{"disambiguationData":[TD([[subQ2,-1.0]])],"derivedFrom":subQ1}),1.0]])]});}
            var Q3;
            {var subQ0=sQuery(id+"F22.wireOp",EDGE,"E55.left");var subQ1=sQuery(id+"F22.wireOp",EDGE,"E55.top");var subQ2=makeQuery(id+"F22.imprint","INTERSECT",VERTEX,{"derivedFrom":[subQ1,subQ0]});Q3=makeQuery(id+"F22.imprint","IMPRINT",FACE,{"disambiguationData":[TD([[makeQuery(id+"F22.imprint","IMPRINT",EDGE,{"disambiguationData":[TD([[subQ2,-1.0]])],"derivedFrom":subQ1}),-1.0]])]});}
            extrude(context, id + "F23", {"entities" : qUnion([Q0, Q1, Q2, Q3]), "operationType" : NewBodyOperationType.REMOVE, "endBound" : BoundingType.THROUGH_ALL, "oppositeDirection" : true, "depth" : 25 * mm});
        }
    });
